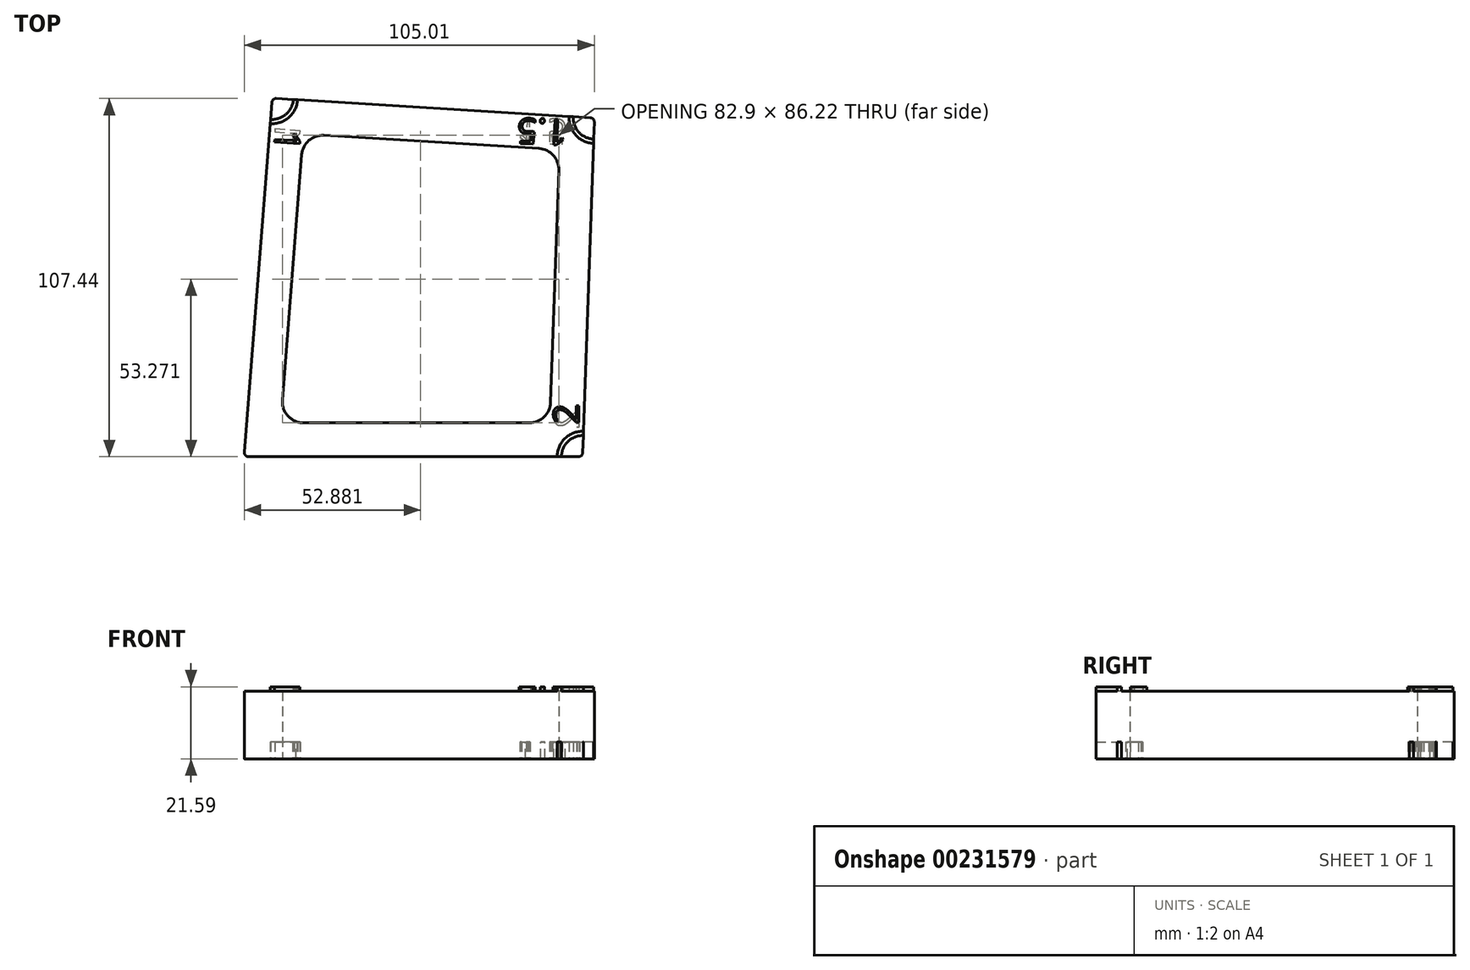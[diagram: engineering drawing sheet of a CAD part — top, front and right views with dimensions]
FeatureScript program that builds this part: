
annotation { "Feature Type Name" : "Feature", "Feature Type Description" : "" }
export const myFeature = defineFeature(function(context is Context, id is Id, definition is map)
    precondition{}
    {
        {
            var Q0;
            Q0=qCreatedBy(makeId("Top.planeOp"),FACE);
            var sketch = newSketch(context, id + "F0", { "sketchPlane" : qUnion([Q0])});
            skLineSegment(sketch, "E0", {"start": v(0, 0) * mm, "end": v(-101.6, 0) * mm});
            skLineSegment(sketch, "E1", {"start": v(-101.6, 0) * mm, "end": v(-93.14, 107.51) * mm});
            skLineSegment(sketch, "E2", {"start": v(-93.14, 107.51) * mm, "end": v(3.55, 101.6) * mm});
            skLineSegment(sketch, "E3", {"start": v(3.55, 101.6) * mm, "end": v(0, 0) * mm});
            skLineSegment(sketch, "E4.0", {"start": v(-77.56, 96.38) * mm, "end": v(-13.13, 92.44) * mm});
            skLineSegment(sketch, "E4.1", {"start": v(-90.07, 17) * mm, "end": v(-84.28, 90.54) * mm});
            skLineSegment(sketch, "E4.2", {"start": v(-15.94, 10.16) * mm, "end": v(-83.74, 10.16) * mm});
            skLineSegment(sketch, "E4.3", {"start": v(-7.17, 85.88) * mm, "end": v(-9.6, 16.29) * mm});
            skPoint(sketch, "E5.visualSharp", {"position": v(-83.8, 96.76) * mm});
            skArc(sketch, "E5.filletArc", {"start": v(-77.56, 96.38) * mm, "mid": v(-82.12, 94.84) * mm, "end": v(-84.28, 90.54) * mm});
            skPoint(sketch, "E6.visualSharp", {"position": v(-6.95, 92.06) * mm});
            skArc(sketch, "E6.filletArc", {"start": v(-7.17, 85.88) * mm, "mid": v(-8.81, 90.37) * mm, "end": v(-13.13, 92.44) * mm});
            skPoint(sketch, "E7.visualSharp", {"position": v(-9.81, 10.16) * mm});
            skArc(sketch, "E7.filletArc", {"start": v(-15.94, 10.16) * mm, "mid": v(-11.53, 11.94) * mm, "end": v(-9.6, 16.29) * mm});
            skPoint(sketch, "E8.visualSharp", {"position": v(-90.6, 10.16) * mm});
            skArc(sketch, "E8.filletArc", {"start": v(-90.07, 17) * mm, "mid": v(-88.4, 12.2) * mm, "end": v(-83.74, 10.16) * mm});
            skSolve(sketch);
        }
        {
            var Q0;
            Q0=makeQuery(id+"F0.imprint","IMPRINT",FACE,{"disambiguationData":[TD([[makeQuery(id+"F0.imprint","IMPRINT",EDGE,{"derivedFrom":sQuery(id+"F0.wireOp",EDGE,"E0")}),-1.0]])]});
            extrude(context, id + "F1", {"entities" : qUnion([Q0]), "depth" : 20.32 * mm});
        }
        {
            var Q0;
            Q0=makeQuery(id+"F1.opExtrude","CAP_FACE",FACE,{"disambiguationData":[OSD([sQuery(id+"F0.wireOp",EDGE,"E0"),sQuery(id+"F0.wireOp",EDGE,"E1"),sQuery(id+"F0.wireOp",EDGE,"E2"),sQuery(id+"F0.wireOp",EDGE,"E3"),sQuery(id+"F0.wireOp",EDGE,"E4.0"),sQuery(id+"F0.wireOp",EDGE,"E4.1"),sQuery(id+"F0.wireOp",EDGE,"E4.2"),sQuery(id+"F0.wireOp",EDGE,"E4.3"),sQuery(id+"F0.wireOp",EDGE,"E5.filletArc"),sQuery(id+"F0.wireOp",EDGE,"E6.filletArc"),sQuery(id+"F0.wireOp",EDGE,"E7.filletArc"),sQuery(id+"F0.wireOp",EDGE,"E8.filletArc")])],"isStart":false});
            var sketch = newSketch(context, id + "F2", { "sketchPlane" : qUnion([Q0])});
            skText(sketch, "E9", { "text": "1", "fontName": "OpenSans-Regular.ttf"});
            skLineSegment(sketch, "E10.0", {"start": v(-86.8, 107.13) * mm, "end": v(-85.53, 107.05) * mm});
            skLineSegment(sketch, "E11.0", {"start": v(-93.74, 99.92) * mm, "end": v(-93.64, 101.18) * mm});
            skArc(sketch, "E12", {"start": v(-85.53, 107.05) * mm, "mid": v(-88.14, 101.76) * mm, "end": v(-93.74, 99.92) * mm});
            skArc(sketch, "E13.0", {"start": v(-86.8, 107.13) * mm, "mid": v(-88.97, 102.72) * mm, "end": v(-93.64, 101.18) * mm});
            skPoint(sketch, "E14.orphan", {"position": v(-101.6, 0) * mm});
            skPoint(sketch, "E15.orphan", {"position": v(3.55, 101.6) * mm});
            skArc(sketch, "E16", {"start": v(-4.06, 102.07) * mm, "mid": v(-2.1, 96.48) * mm, "end": v(3.28, 93.98) * mm});
            skArc(sketch, "E17.0", {"start": v(-2.8, 101.99) * mm, "mid": v(-1.15, 97.33) * mm, "end": v(3.33, 95.25) * mm});
            skLineSegment(sketch, "E18.0", {"start": v(-93.14, 107.51) * mm, "end": v(-85.53, 107.05) * mm});
            skLineSegment(sketch, "E19.0", {"start": v(3.33, 95.25) * mm, "end": v(3.28, 93.98) * mm});
            skLineSegment(sketch, "E20.trimOffspring", {"start": v(-4.06, 102.07) * mm, "end": v(-2.8, 101.99) * mm});
            skPoint(sketch, "E21.orphan", {"position": v(0, 0) * mm});
            skArc(sketch, "E22", {"start": v(0.27, 7.62) * mm, "mid": v(-5.3, 5.48) * mm, "end": v(-7.62, 0) * mm});
            skArc(sketch, "E23.0", {"start": v(0.22, 6.35) * mm, "mid": v(-4.41, 4.57) * mm, "end": v(-6.35, 0) * mm});
            skLineSegment(sketch, "E24.0", {"start": v(-6.35, 0) * mm, "end": v(-7.62, 0) * mm});
            skLineSegment(sketch, "E25.0", {"start": v(3.55, 101.6) * mm, "end": v(0.22, 6.35) * mm});
            skText(sketch, "E26", { "text": "1.5", "fontName": "OpenSans-Regular.ttf"});
            skText(sketch, "E27", { "text": "2", "fontName": "OpenSans-Regular.ttf"});
            const initialGuessF2  = {"E9": [-0.0922, 0.09803, -0.06105, -0.99813, 0.00762], "E26": [-0.00463, 0.10099, -0.9994, 0.0349, 0.00762], "E27": [-0.00118, 0.0098, 0, 1, 0.00762]};
            skSetInitialGuess(sketch, initialGuessF2);
            skSolve(sketch);
        }
        {
            var Q0;
            Q0=qSketchRegion(id+"F2",true);
            extrude(context, id + "F3", {"entities" : qUnion([Q0]), "operationType" : NewBodyOperationType.ADD, "depth" : 1.27 * mm});
        }
        {
            var Q0;
            Q0=makeQuery(id+"F1.opExtrude","CAP_FACE",FACE,{"disambiguationData":[OSD([sQuery(id+"F0.wireOp",EDGE,"E0"),sQuery(id+"F0.wireOp",EDGE,"E1"),sQuery(id+"F0.wireOp",EDGE,"E2"),sQuery(id+"F0.wireOp",EDGE,"E3"),sQuery(id+"F0.wireOp",EDGE,"E4.0"),sQuery(id+"F0.wireOp",EDGE,"E4.1"),sQuery(id+"F0.wireOp",EDGE,"E4.2"),sQuery(id+"F0.wireOp",EDGE,"E4.3"),sQuery(id+"F0.wireOp",EDGE,"E5.filletArc"),sQuery(id+"F0.wireOp",EDGE,"E6.filletArc"),sQuery(id+"F0.wireOp",EDGE,"E7.filletArc"),sQuery(id+"F0.wireOp",EDGE,"E8.filletArc")])],"isStart":true});
            var sketch = newSketch(context, id + "F4", { "sketchPlane" : qUnion([Q0])});
            skArc(sketch, "E28.0", {"start": v(0.22, -6.35) * mm, "mid": v(-4.41, -4.57) * mm, "end": v(-6.35, 0) * mm});
            skArc(sketch, "E29.0", {"start": v(0.27, -7.62) * mm, "mid": v(-5.3, -5.48) * mm, "end": v(-7.62, 0) * mm});
            skLineSegment(sketch, "E30.0", {"start": v(-6.35, 0) * mm, "end": v(-7.62, 0) * mm});
            skLineSegment(sketch, "E31.0", {"start": v(0.27, -7.62) * mm, "end": v(0.22, -6.35) * mm});
            skArc(sketch, "E32.0", {"start": v(-86.8, -107.13) * mm, "mid": v(-88.97, -102.72) * mm, "end": v(-93.64, -101.18) * mm});
            skArc(sketch, "E33.0", {"start": v(-85.53, -107.05) * mm, "mid": v(-88.14, -101.76) * mm, "end": v(-93.74, -99.92) * mm});
            skLineSegment(sketch, "E34.0", {"start": v(-93.74, -99.92) * mm, "end": v(-93.64, -101.18) * mm});
            skLineSegment(sketch, "E35.0", {"start": v(-86.8, -107.13) * mm, "end": v(-85.53, -107.05) * mm});
            skArc(sketch, "E36.0.0", {"start": v(3.33, -95.25) * mm, "mid": v(-1.15, -97.33) * mm, "end": v(-2.8, -101.99) * mm});
            skLineSegment(sketch, "E36.0.1", {"start": v(-2.8, -101.99) * mm, "end": v(-4.06, -102.07) * mm});
            skArc(sketch, "E36.0.2", {"start": v(-4.06, -102.07) * mm, "mid": v(-2.1, -96.48) * mm, "end": v(3.28, -93.98) * mm});
            skLineSegment(sketch, "E36.0.3", {"start": v(3.28, -93.98) * mm, "end": v(3.33, -95.25) * mm});
            skText(sketch, "E37", { "text": "1", "fontName": "OpenSans-Regular.ttf"});
            skText(sketch, "E38", { "text": "1.5\n", "fontName": "OpenSans-Regular.ttf"});
            skText(sketch, "E39", { "text": "2", "fontName": "OpenSans-Regular.ttf"});
            const initialGuessF4  = {"E37": [-0.09257, -0.09462, 0.07846, -0.99692, 0.00762], "E38": [-0.01938, -0.10198, 0.99813, 0.06105, 0.00762], "E39": [-0.00084, -0.01434, -0.0349, 0.9994, 0.00762]};
            skSetInitialGuess(sketch, initialGuessF4);
            skSolve(sketch);
        }
        {
            var Q0;
            Q0=qSketchRegion(id+"F4",true);
            extrude(context, id + "F5", {"entities" : qUnion([Q0]), "operationType" : NewBodyOperationType.REMOVE, "oppositeDirection" : true, "depth" : 5.08 * mm});
        }
        {
            var Q0;
            Q0=makeQuery(id+"F1.opExtrude","SWEPT_EDGE",EDGE,{"disambiguationData":[OSD([sQuery(id+"F0.wireOp",EDGE,"E0"),sQuery(id+"F0.wireOp",EDGE,"E1")])]});
            var Q1;
            Q1=makeQuery(id+"F1.opExtrude","SWEPT_EDGE",EDGE,{"disambiguationData":[OSD([sQuery(id+"F0.wireOp",EDGE,"E1"),sQuery(id+"F0.wireOp",EDGE,"E2")])]});
            var Q2;
            Q2=makeQuery(id+"F1.opExtrude","SWEPT_EDGE",EDGE,{"disambiguationData":[OSD([sQuery(id+"F0.wireOp",EDGE,"E2"),sQuery(id+"F0.wireOp",EDGE,"E3")])]});
            var Q3;
            Q3=makeQuery(id+"F1.opExtrude","SWEPT_EDGE",EDGE,{"disambiguationData":[OSD([sQuery(id+"F0.wireOp",EDGE,"E0"),sQuery(id+"F0.wireOp",EDGE,"E3")])]});
            fillet(context, id + "F6", {"entities" : qUnion([Q0, Q1, Q2, Q3]), "radius" : 1.27 * mm, "tangentPropagation" : true, "allowEdgeOverflow" : false});
        }
    });
